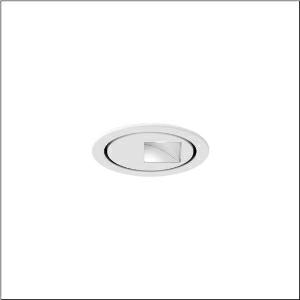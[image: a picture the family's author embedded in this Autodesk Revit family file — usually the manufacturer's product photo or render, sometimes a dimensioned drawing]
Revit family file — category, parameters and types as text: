
# Revit family: lunis_11_micro_round_51dj11b71wg21
name_source: partatom
category: Lighting Fixtures
units: mm (PartAtom-declared; Revit-internal decimal feet)

## family parameters
Cut with Voids When Loaded = No
Host = Face
Light Source = No
Part Type = Normal
Room Calculation Point = No
Round Connector Dimension = Use Diameter
Shared = No

## types (1)
- Lunis 11 micro round (1 x LED 4000K / CRI = 80 (unbekannt), 1400 lm, 4000K)
    Apparent Load = 20 VA
    CIE Flux Codes = 42 75 96 100 100
    Color Rendering = 80
    Color Temperature = 4000K
    Default Elevation = 1800 mm
    Description = Lunis 11 micro round, downlight, light control with wallwasher, of highly reflective aluminium, highly specular, light emission: direct distribution, LED rated luminous flux: 1.400lm, light colour: 840, with terminal, 3-pole, mains connection: 220..230V, AC, 50/60Hz, LED module, of aluminium, highly specular, white, diameter: 114mm, clamping range: 1..40mm, recessing ring, of plastic, traffic white (RAL 9016), protection rating (complete): IP20, insulation class (complete): insulation class II (safety insulation), certification: CE, permissible ambient temperature for indoor applications: 0..+35°C, packaging unit: 1 piece
    Height = 0 mm  [stored 0 ft]
    Lamp = 1 x LED 4000K / CRI >= 80 (unbekannt)
    Lamp Light Flux = 1400 lm
    Lamp count = 1
    Length = 114 mm
    Luminous efficacy = 71 lm/W
    Manufacturer = Siteco
    ModVariant = No
    Model = 51DJ11B71WG21
    Mounting Place = Ceiling
    Mounting Type = Recessed
    Number of Poles = 1
    OnlyDefault = Yes
    Power Factor = 1
    Product Name = Lunis 11 micro round
    Product group = downlight
    ProductGroupID = 400
    Protection Class = Protection class II
    Protection Degree = IP 20
    RLX_Detail_Level = 1
    RLX_Emergency_Light_Flux = 0 lm
    RLX_Emergency_Type = 0
    RLX_Emergency_Type_DB = No
    RlxData = <blob elided: 40345 chars, md5=afb0f56e>
    Socket = socket
    Standby Power = 0 W
    System Light Flux = 1400 lm
    System Power = 20 W
    Type Comments = Product without accessories
    Type Image = l_1004773.jpg
    URL = http://relux.com
    VarID = ---
    Voltage = 0 V
    Weight = 0.00 kg
    Width = 114 mm

note: [stored X ft] marks values corroborated as IEEE doubles in the binary element streams (Revit-internal decimal feet)

## geometry (parser evidence)
native form markers: Blend x4, Sweep x9
no freeform markers — native parametric forms only
